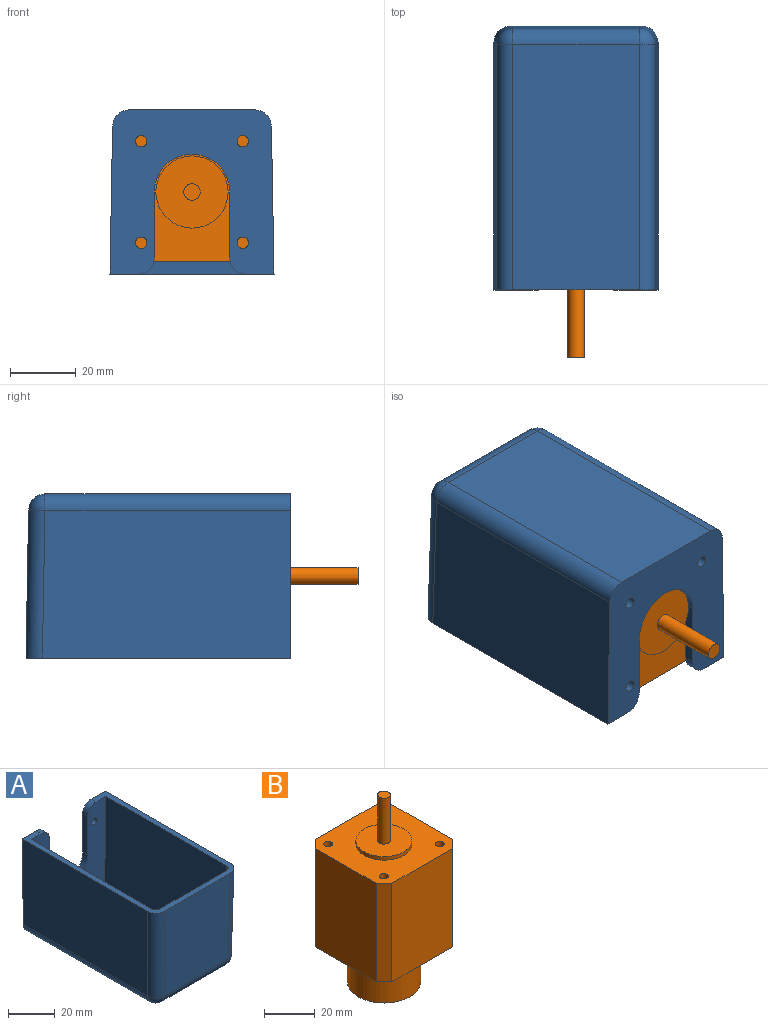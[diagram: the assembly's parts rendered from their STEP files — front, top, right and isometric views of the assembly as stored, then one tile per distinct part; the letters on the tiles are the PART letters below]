
ASSEMBLY  parts=2 mates=1
PART A: 34 faces, bbox 50x80.5x50 mm
  f0: plane 20x3mm, normal (1,0,0), area 60mm2, adj f1,f8,f13,f14
  f1: cylinder r=5mm len=5mm, axis (0,1,0), area 23.6mm2, adj f0,f5,f13,f14
  f2: plane 75.5x45.09mm, normal (-1,0,-0.02), area 3386.9mm2, adj f5,f14,f21,f33
  f3: plane 74.71x38.43mm, normal (0,0,-1), area 2871.1mm2, adj f14,f29,f31,f33
  f4: plane 75.5x45.09mm, normal (1,0,-0.02), area 3386.9mm2, adj f5,f14,f20,f29
  f5: plane 80.5x50mm, normal (0,0,1), area 543mm2, adj f1,f2,f4,f6,f13,f14,f16,f17
  f6: cylinder r=5mm len=5mm, axis (0,1,0), area 23.6mm2, adj f5,f7,f13,f14
  f7: plane 20x3mm, normal (-1,0,0), area 60mm2, adj f6,f8,f13,f14
  f8: cylinder r=11.5mm len=23mm, axis (0,1,0), area 108.4mm2, adj f0,f7,f13,f14
  f9: cylinder r=1.75mm len=3.5mm, axis (0,1,0), area 33mm2, adj f13,f14
  f10: cylinder r=1.75mm len=3.5mm, axis (0,1,0), area 33mm2, adj f13,f14
  f11: cylinder r=1.75mm len=3.5mm, axis (0,1,0), area 33mm2, adj f13,f14
  f12: cylinder r=1.75mm len=3.5mm, axis (0,1,0), area 33mm2, adj f13,f14
  f13: plane 47.5x45mm, normal (0,-1,0), area 1263.6mm2, adj f0,f1,f5,f6,f7,f8,f9,f10
  f14: plane 50x50mm, normal (0,1,0), area 1614.1mm2, adj f0,f1,f2,f3,f4,f5,f6,f7
  f15: plane 71.71x38.43mm, normal (0,0,1), area 2755.9mm2, adj f13,f23,f25,f26
  f16: plane 72.5x45.04mm, normal (1,0,0.02), area 3248.5mm2, adj f5,f13,f22,f23
  f17: plane 72.5x45.04mm, normal (-1,0,0.02), area 3248.5mm2, adj f5,f13,f26,f28
  f18: plane 45.04x40mm, normal (0,1,0.02), area 1766.6mm2, adj f5,f22,f25,f28
  f19: plane 45.09x40mm, normal (0,-1,-0.02), area 1768.3mm2, adj f5,f20,f21,f31
  f20: cylinder r=5mm len=45.16mm, axis (-0.02,0.02,-1), area 354.3mm2, adj f4,f5,f19,f30
  f21: cylinder r=5mm len=45.16mm, axis (0.02,0.02,-1), area 354.3mm2, adj f2,f5,f19,f32
  f22: cylinder r=2.5mm len=45.08mm, axis (0.02,0.02,-1), area 177mm2, adj f5,f16,f18,f24
  f23: cylinder r=2.5mm len=71.71mm, axis (0,-1,0), area 278.5mm2, adj f13,f15,f16,f24
  f24: sphere r=2.5mm, area 9.6mm2, adj f22,f23,f25
  f25: cylinder r=2.5mm len=38.43mm, axis (1,0,0), area 149.2mm2, adj f15,f18,f24,f27
  f26: cylinder r=2.5mm len=71.71mm, axis (0,-1,0), area 278.5mm2, adj f13,f15,f17,f27
  f27: sphere r=2.5mm, area 9.6mm2, adj f25,f26,f28
  f28: cylinder r=2.5mm len=45.08mm, axis (0.02,-0.02,1), area 177mm2, adj f5,f17,f18,f27
  f29: cylinder r=5mm len=74.71mm, axis (0,-1,0), area 580.3mm2, adj f3,f4,f14,f30
  f30: sphere r=5mm, area 38.4mm2, adj f20,f29,f31
  f31: cylinder r=5mm len=38.43mm, axis (1,0,0), area 298.5mm2, adj f3,f19,f30,f32
  f32: sphere r=5mm, area 38.4mm2, adj f21,f31,f33
  f33: cylinder r=5mm len=74.71mm, axis (0,1,0), area 580.3mm2, adj f2,f3,f14,f32
PART B: 24 faces, bbox 42.3x42.3x90 mm
  f0: plane 47.3x33.5mm, normal (0,-1,0), area 1584.6mm2, adj f4,f5,f7,f9
  f1: plane 47.3x33.5mm, normal (1,0,0), area 1584.6mm2, adj f4,f5,f6,f7
  f2: plane 47.3x33.5mm, normal (0,1,0), area 1584.6mm2, adj f4,f5,f6,f8
  f3: plane 47.3x33.5mm, normal (-1,0,0), area 1584.6mm2, adj f4,f5,f8,f9
  f4: plane 42.3x42.3mm, normal (0,0,1), area 1332mm2, adj f0,f1,f2,f3,f6,f7,f8,f9
  f5: plane 42.3x42.3mm, normal (0,0,-1), area 1101.4mm2, adj f0,f1,f2,f3,f6,f7,f8,f9
  f6: plane 47.3x4.4mm, normal (0.71,0.71,0), area 294.3mm2, adj f1,f2,f4,f5
  f7: plane 47.3x4.4mm, normal (0.71,-0.71,0), area 294.3mm2, adj f0,f1,f4,f5
  f8: plane 47.3x4.4mm, normal (-0.71,0.71,0), area 294.3mm2, adj f2,f3,f4,f5
  f9: plane 47.3x4.4mm, normal (-0.71,-0.71,0), area 294.3mm2, adj f0,f3,f4,f5
  f10: cylinder r=11mm len=22mm, axis (0,0,-1), area 117.5mm2, adj f4,f11
  f11: plane 22x22mm, normal (0,0,1), area 360.5mm2, adj f10,f12
  f12: cylinder r=2.5mm len=22mm, axis (0,0,-1), area 345.6mm2, adj f11,f13
  f13: plane 5x5mm, normal (0,0,1), area 19.6mm2, adj f12
  f14: cylinder r=1.75mm len=10mm, axis (0,0,1), area 110mm2, adj f4,f15
  f15: plane 3.5x3.5mm, normal (0,0,1), area 9.6mm2, adj f14
  f16: cylinder r=1.75mm len=10mm, axis (0,0,1), area 110mm2, adj f4,f17
  f17: plane 3.5x3.5mm, normal (0,0,1), area 9.6mm2, adj f16
  f18: cylinder r=1.75mm len=10mm, axis (0,0,1), area 110mm2, adj f4,f19
  f19: plane 3.5x3.5mm, normal (0,0,1), area 9.6mm2, adj f18
  f20: cylinder r=1.75mm len=10mm, axis (0,0,1), area 110mm2, adj f4,f21
  f21: plane 3.5x3.5mm, normal (0,0,1), area 9.6mm2, adj f20
  f22: cylinder r=14.38mm len=28.75mm, axis (0,0,1), area 1716.1mm2, adj f5,f23
  f23: plane 28.75x28.75mm, normal (0,0,-1), area 649.2mm2, adj f22
PLACE A rot(axis=(-1,0,0),180deg) t=(0,20.7,25)mm
PLACE B rot(axis=(1,0,0),90deg) t=(0,71,0)mm
MATE fastened A.f8 <-> B.f10  axis (0,1,0) through (0,23.7,0)mm
